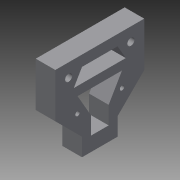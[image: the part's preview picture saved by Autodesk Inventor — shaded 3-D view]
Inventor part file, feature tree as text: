
AUTODESK INVENTOR PART (.ipt)
format: ipt  version: 2013 (Build 170138000, 138)  size: 209,920 bytes
history: native  units: mm
features: sketch x7, extrude x5, hole x2, other x1, pattern_circular x1
ambient origin geometry x8: Origin, YZ Plane, XZ Plane, XY Plane, X Axis, Y Axis, Z Axis, Center Point
feature tree (16):
  other  "ソリッド1"
  extrude  "押し出し1"  Depth=100.0mm
  extrude  "押し出し2"  Depth=100.0mm
  extrude  "押し出し5"  Depth=50.0mm
  hole  "穴1"  [1 undecoded]
  pattern_circular  "円形状パターン2"  [2 undecoded]
  hole  "穴2"  [1 undecoded]
  extrude  "押し出し6"  TaperAngle=135.0deg  [1 undecoded]
  extrude  "押し出し7"  Depth=25.0mm
  sketch  "スケッチ1"
  sketch  "スケッチ2"
  sketch  "スケッチ3"
  sketch  "スケッチ4"
  sketch  "スケッチ5"
  sketch  "スケッチ6"
  sketch  "スケッチ7"
note: 5 required parameter values undecoded (feature->parameter linkage not recoverable at this tier; creation-order binding heuristic only, values carry confidence <= 0.55)
